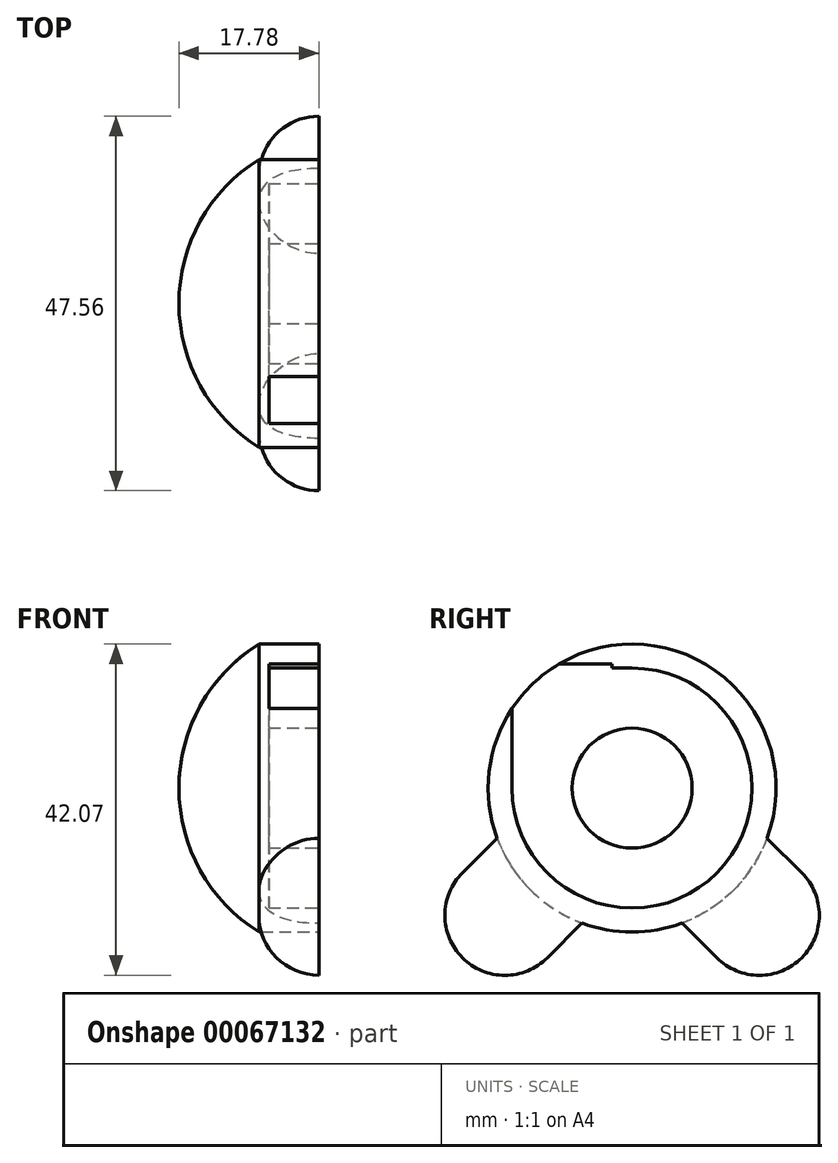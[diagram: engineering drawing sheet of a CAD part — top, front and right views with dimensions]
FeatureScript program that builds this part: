
annotation { "Feature Type Name" : "Feature", "Feature Type Description" : "" }
export const myFeature = defineFeature(function(context is Context, id is Id, definition is map)
    precondition{}
    {
        {
            var Q0;
            Q0=qCreatedBy(makeId("Right.planeOp"),FACE);
            var sketch = newSketch(context, id + "F0", { "sketchPlane" : qUnion([Q0])});
            skLineSegment(sketch, "E0", {"start": v(-25.4, 15.24) * mm, "end": v(0, 15.24) * mm});
            skArc(sketch, "E1", {"start": v(-15.24, 0) * mm, "mid": v(10.78, -10.78) * mm, "end": v(0, 15.24) * mm});
            skLineSegment(sketch, "E2", {"start": v(-25.4, 15.24) * mm, "end": v(-25.4, 10.16) * mm});
            skLineSegment(sketch, "E3", {"start": v(-25.4, 10.16) * mm, "end": v(-15.24, 10.16) * mm});
            skLineSegment(sketch, "E4", {"start": v(-15.24, 10.16) * mm, "end": v(-15.24, 0) * mm});
            skLineSegment(sketch, "E5.top", {"start": v(-15.24, 15.75) * mm, "end": v(-2.54, 15.75) * mm});
            skLineSegment(sketch, "E5.left", {"start": v(-15.24, 15.24) * mm, "end": v(-15.24, 15.75) * mm});
            skLineSegment(sketch, "E5.right", {"start": v(-2.54, 15.24) * mm, "end": v(-2.54, 15.75) * mm});
            skCircle(sketch, "E6", {"center": v(0, 0) * mm, "radius": 7.62 * mm});
            skSolve(sketch);
        }
        {
            var Q0;
            Q0=qCreatedBy(makeId("Front.planeOp"),FACE);
            var sketch = newSketch(context, id + "F1", { "sketchPlane" : qUnion([Q0])});
            skLineSegment(sketch, "E7.left", {"start": v(0, 18.29) * mm, "end": v(0, 0) * mm});
            skLineSegment(sketch, "E8.MirrorCS", {"start": v(-17.78, 0) * mm, "end": v(-7.62, 0) * mm});
            skArc(sketch, "E9.MirrorCS", {"start": v(-17.78, 0) * mm, "mid": v(-15.07, 10.46) * mm, "end": v(-7.62, 18.29) * mm});
            skLineSegment(sketch, "E10.MirrorCS", {"start": v(-7.62, 18.29) * mm, "end": v(-7.62, 0) * mm});
            skLineSegment(sketch, "E11.MirrorCS", {"start": v(0, 0) * mm, "end": v(-7.62, 0) * mm});
            skLineSegment(sketch, "E12.MirrorCS", {"start": v(0, 18.29) * mm, "end": v(-7.62, 18.29) * mm});
            skSolve(sketch);
        }
        {
            var Q0;
            Q0=qSketchRegion(id+"F1",true);
            var Q1;
            Q1=sQuery(id+"F1.wireOp",EDGE,"E11.MirrorCS");
            revolve(context, id + "F2", {"entities" : qUnion([Q0]), "axis" : qUnion([Q1]), "revolveType" : RevolveType.FULL});
        }
        {
            var Q0;
            Q0=qCreatedBy(makeId("Right.planeOp"),FACE);
            var sketch = newSketch(context, id + "F3", { "sketchPlane" : qUnion([Q0])});
            skLineSegment(sketch, "E13", {"start": v(0, 0) * mm, "end": v(-16.16, -16.16) * mm});
            skLineSegment(sketch, "E14.MirrorCS", {"start": v(0, 0) * mm, "end": v(16.16, -16.16) * mm});
            skLineSegment(sketch, "E15", {"start": v(-12.57, -1.8) * mm, "end": v(-21.55, -10.78) * mm});
            skLineSegment(sketch, "E16", {"start": v(-21.55, -10.78) * mm, "end": v(-16.16, -16.16) * mm});
            skArc(sketch, "E17", {"start": v(-21.55, -10.78) * mm, "mid": v(-23.78, -16.16) * mm, "end": v(-21.55, -21.55) * mm});
            skLineSegment(sketch, "E18", {"start": v(-16.16, -16.16) * mm, "end": v(-21.55, -21.55) * mm});
            skLineSegment(sketch, "E19", {"start": v(-12.57, -1.8) * mm, "end": v(-7.18, -7.18) * mm});
            skLineSegment(sketch, "E20.MirrorCS", {"start": v(12.57, -1.8) * mm, "end": v(7.18, -7.18) * mm});
            skLineSegment(sketch, "E21.MirrorCS", {"start": v(12.57, -1.8) * mm, "end": v(21.55, -10.78) * mm});
            skLineSegment(sketch, "E22.MirrorCS", {"start": v(21.55, -10.78) * mm, "end": v(16.16, -16.16) * mm});
            skLineSegment(sketch, "E23.MirrorCS", {"start": v(16.16, -16.16) * mm, "end": v(21.55, -21.55) * mm});
            skArc(sketch, "E24.MirrorCS", {"start": v(21.55, -10.78) * mm, "mid": v(23.78, -16.16) * mm, "end": v(21.55, -21.55) * mm});
            skSolve(sketch);
        }
        {
            var Q0;
            Q0=makeQuery(id+"F3.imprint","IMPRINT",FACE,{"disambiguationData":[TD([[makeQuery(id+"F3.imprint","IMPRINT",EDGE,{"derivedFrom":sQuery(id+"F3.wireOp",EDGE,"E15")}),1.0]])]});
            var Q1;
            Q1=makeQuery(id+"F3.imprint","IMPRINT",FACE,{"disambiguationData":[TD([[makeQuery(id+"F3.imprint","IMPRINT",EDGE,{"derivedFrom":sQuery(id+"F3.wireOp",EDGE,"E16")}),-1.0]])]});
            var Q2;
            Q2=sQuery(id+"F3.wireOp",EDGE,"E13");
            revolve(context, id + "F4", {"operationType" : NewBodyOperationType.ADD, "entities" : qUnion([Q0, Q1]), "axis" : qUnion([Q2]), "revolveType" : RevolveType.ONE_DIRECTION, "angle" : 180 * degree});
        }
        {
            var Q0;
            {var subQ2=sQuery(id+"F3.wireOp",EDGE,"E20.MirrorCS");Q0=makeQuery(id+"F3.imprint","IMPRINT",FACE,{"disambiguationData":[TD([[makeQuery(id+"F3.imprint","IMPRINT",EDGE,{"derivedFrom":subQ2}),1.0]])]});}
            var Q1;
            Q1=makeQuery(id+"F3.imprint","IMPRINT",FACE,{"disambiguationData":[TD([[makeQuery(id+"F3.imprint","IMPRINT",EDGE,{"derivedFrom":sQuery(id+"F3.wireOp",EDGE,"E22.MirrorCS")}),1.0]])]});
            var Q2;
            Q2=sQuery(id+"F3.wireOp",EDGE,"E14.MirrorCS");
            revolve(context, id + "F5", {"operationType" : NewBodyOperationType.ADD, "entities" : qUnion([Q0, Q1]), "axis" : qUnion([Q2]), "revolveType" : RevolveType.ONE_DIRECTION, "oppositeDirection" : true, "angle" : 180 * degree});
        }
        {
            var Q0;
            Q0=qSketchRegion(id+"F0",true);
            extrude(context, id + "F6", {"entities" : qUnion([Q0]), "operationType" : NewBodyOperationType.REMOVE, "oppositeDirection" : true, "depth" : 6.35 * mm});
        }
    });
